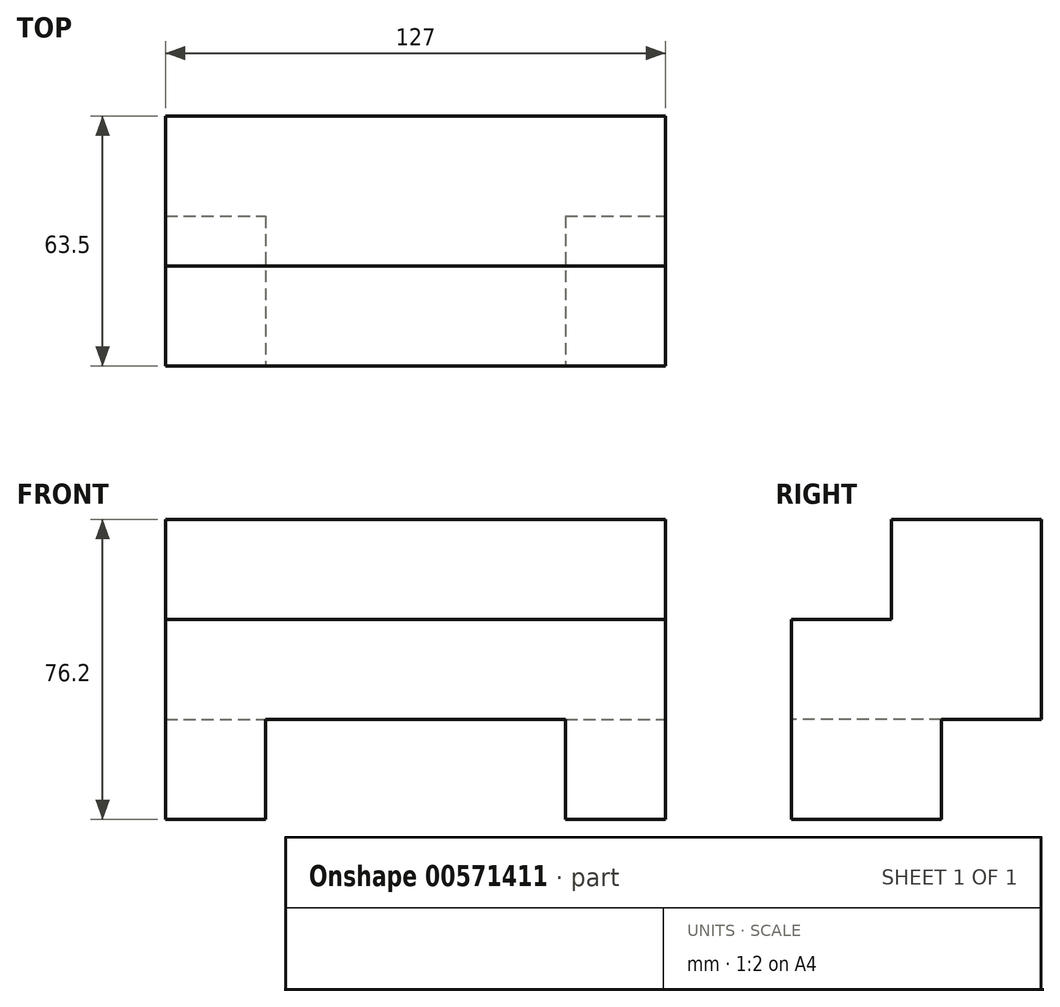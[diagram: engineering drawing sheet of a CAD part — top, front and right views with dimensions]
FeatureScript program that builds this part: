
annotation { "Feature Type Name" : "Feature", "Feature Type Description" : "" }
export const myFeature = defineFeature(function(context is Context, id is Id, definition is map)
    precondition{}
    {
        {
            var Q0;
            Q0=qCreatedBy(makeId("Front.planeOp"),FACE);
            var sketch = newSketch(context, id + "F0", { "sketchPlane" : qUnion([Q0])});
            skLineSegment(sketch, "E0.bottom", {"start": v(-86.03, 18.6) * mm, "end": v(40.97, 18.6) * mm});
            skLineSegment(sketch, "E0.top", {"start": v(-86.03, -57.6) * mm, "end": v(40.97, -57.6) * mm});
            skLineSegment(sketch, "E0.left", {"start": v(-86.03, 18.6) * mm, "end": v(-86.03, -57.6) * mm});
            skLineSegment(sketch, "E0.right", {"start": v(40.97, 18.6) * mm, "end": v(40.97, -57.6) * mm});
            skSolve(sketch);
        }
        {
            var Q0;
            Q0=qSketchRegion(id+"F0",true);
            extrude(context, id + "F1", {"entities" : qUnion([Q0]), "depth" : 63.5 * mm, "offsetDistance" : 25.4 * mm});
        }
        {
            var Q0;
            Q0=makeQuery(id+"F1.opExtrude","CAP_FACE",FACE,{"disambiguationData":[OSD([sQuery(id+"F0.wireOp",EDGE,"E0.bottom"),sQuery(id+"F0.wireOp",EDGE,"E0.top"),sQuery(id+"F0.wireOp",EDGE,"E0.left"),sQuery(id+"F0.wireOp",EDGE,"E0.right")])],"isStart":false});
            var sketch = newSketch(context, id + "F2", { "sketchPlane" : qUnion([Q0])});
            skLineSegment(sketch, "E1", {"start": v(-86.03, -57.6) * mm, "end": v(-60.63, -57.6) * mm});
            skLineSegment(sketch, "E2", {"start": v(-60.63, -57.6) * mm, "end": v(-60.63, -32.2) * mm});
            skLineSegment(sketch, "E3", {"start": v(40.97, -57.6) * mm, "end": v(15.57, -57.6) * mm});
            skLineSegment(sketch, "E4", {"start": v(15.57, -57.6) * mm, "end": v(15.57, -32.2) * mm});
            skLineSegment(sketch, "E5", {"start": v(15.57, -32.2) * mm, "end": v(-60.63, -32.2) * mm});
            skLineSegment(sketch, "E6", {"start": v(-60.63, -57.6) * mm, "end": v(15.57, -57.6) * mm});
            skSolve(sketch);
        }
        {
            var Q0;
            Q0=makeQuery(id+"F2.imprint","IMPRINT",FACE,{"disambiguationData":[TD([[makeQuery(id+"F2.imprint","IMPRINT",EDGE,{"derivedFrom":sQuery(id+"F2.wireOp",EDGE,"E2")}),-1.0]])]});
            extrude(context, id + "F3", {"entities" : qUnion([Q0]), "operationType" : NewBodyOperationType.REMOVE, "endBound" : BoundingType.THROUGH_ALL, "oppositeDirection" : true, "depth" : 25.4 * mm, "offsetDistance" : 25.4 * mm});
        }
        {
            var Q0;
            Q0=makeQuery(id+"F1.opExtrude","SWEPT_FACE",FACE,{"disambiguationData":[OSD([sQuery(id+"F0.wireOp",EDGE,"E0.right")])]});
            var sketch = newSketch(context, id + "F4", { "sketchPlane" : qUnion([Q0])});
            skLineSegment(sketch, "E7", {"start": v(-63.5, 18.6) * mm, "end": v(-38.1, 18.6) * mm});
            skLineSegment(sketch, "E8", {"start": v(-38.1, 18.6) * mm, "end": v(-38.1, -6.8) * mm});
            skLineSegment(sketch, "E9", {"start": v(-38.1, -6.8) * mm, "end": v(-63.5, -6.8) * mm});
            skLineSegment(sketch, "E10", {"start": v(-63.5, -6.8) * mm, "end": v(-63.5, 18.6) * mm});
            skLineSegment(sketch, "E11", {"start": v(0, -57.6) * mm, "end": v(0, -32.2) * mm});
            skLineSegment(sketch, "E12", {"start": v(0, -32.2) * mm, "end": v(-25.4, -32.2) * mm});
            skLineSegment(sketch, "E13", {"start": v(-25.4, -32.2) * mm, "end": v(-25.4, -57.6) * mm});
            skLineSegment(sketch, "E14", {"start": v(-25.4, -57.6) * mm, "end": v(0, -57.6) * mm});
            skSolve(sketch);
        }
        {
            var Q0;
            Q0=makeQuery(id+"F4.imprint","IMPRINT",FACE,{"disambiguationData":[TD([[makeQuery(id+"F4.imprint","IMPRINT",EDGE,{"derivedFrom":sQuery(id+"F4.wireOp",EDGE,"E11")}),-1.0]])]});
            var Q1;
            Q1=makeQuery(id+"F4.imprint","IMPRINT",FACE,{"disambiguationData":[TD([[makeQuery(id+"F4.imprint","IMPRINT",EDGE,{"derivedFrom":sQuery(id+"F4.wireOp",EDGE,"E7")}),-1.0]])]});
            extrude(context, id + "F5", {"entities" : qUnion([Q0, Q1]), "operationType" : NewBodyOperationType.REMOVE, "endBound" : BoundingType.THROUGH_ALL, "oppositeDirection" : true, "depth" : 25.4 * mm, "offsetDistance" : 25.4 * mm});
        }
    });
